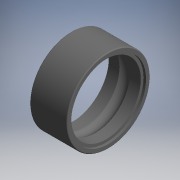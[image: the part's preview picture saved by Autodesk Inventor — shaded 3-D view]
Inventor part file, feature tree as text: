
AUTODESK INVENTOR PART (.ipt)
format: ipt  version: 2017.3 (Build 213256000, 256)  size: 141,312 bytes
history: native  units: mm (DEFAULTED — no unit token found)
features: other x14, revolve x1, sketch x1
ambient origin geometry x8: Origin, YZ Plane, XZ Plane, XY Plane, X Axis, Y Axis, Z Axis, Center Point
bodies: Solid1 (feature_tree)
feature tree (16):
  revolve  "Revolution1"  [1 undecoded]
  other  "ip_st_or_1_XY"
  other  "ip_st_or_1_YZ"
  other  "ip_st_or_1_ZX"
  other  "ip_st_or_1_X"
  other  "ip_st_or_1_Y"
  other  "ip_st_or_1_Z"
  other  "ip_st_or_1_Center"
  other  "ip_st_or_2_XY"
  other  "ip_st_or_2_YZ"
  other  "ip_st_or_2_ZX"
  other  "ip_st_or_2_X"
  other  "ip_st_or_2_Y"
  other  "ip_st_or_2_Z"
  other  "ip_st_or_2_Center"
  sketch  "Sketch_1"  dims[d0=360.0deg d1=0.0mm d2=0.0mm]
note: 1 required parameter value undecoded (feature->parameter linkage not recoverable at this tier; creation-order binding heuristic only, values carry confidence <= 0.55)
